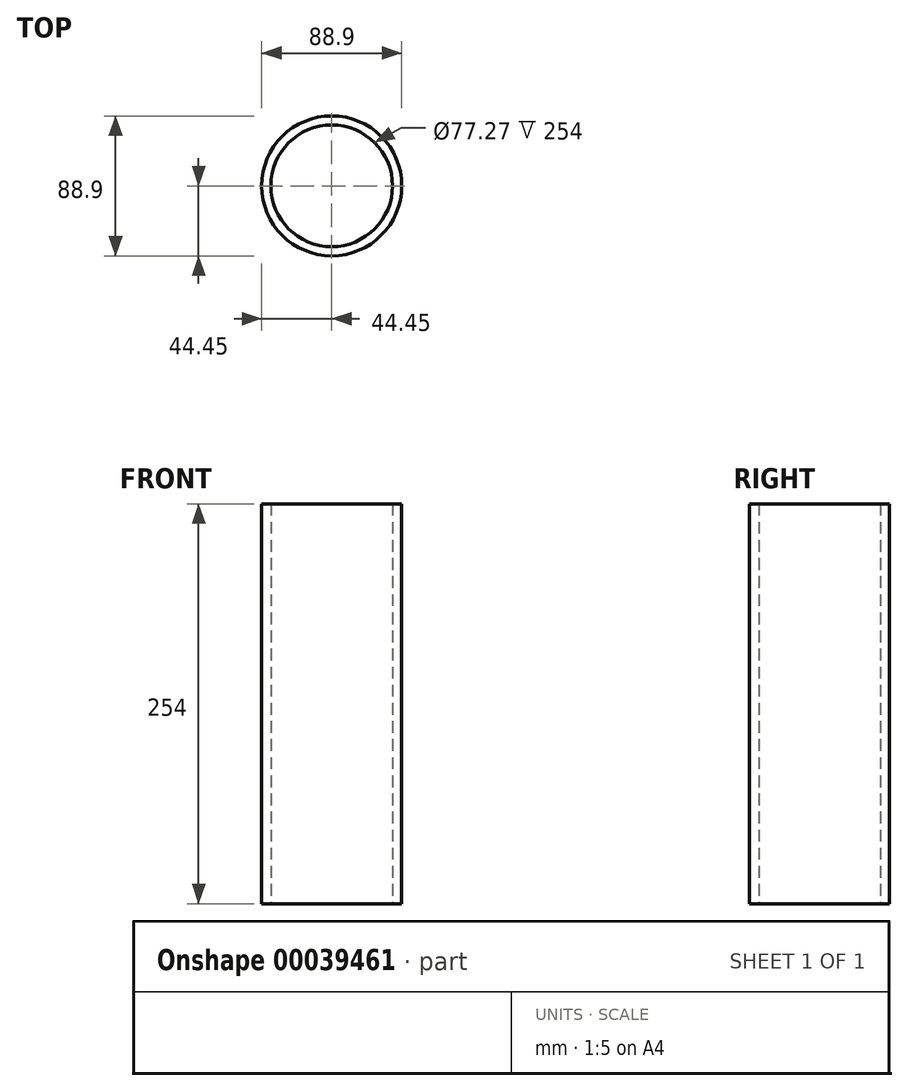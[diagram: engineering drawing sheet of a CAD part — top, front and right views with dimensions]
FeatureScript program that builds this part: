
annotation { "Feature Type Name" : "Feature", "Feature Type Description" : "" }
export const myFeature = defineFeature(function(context is Context, id is Id, definition is map)
    precondition{}
    {
        {
            var Q0;
            Q0=qCreatedBy(makeId("Top.planeOp"),FACE);
            var sketch = newSketch(context, id + "F0", { "sketchPlane" : qUnion([Q0])});
            skCircle(sketch, "E0", {"center": v(0, 0) * mm, "radius": 38.63 * mm});
            skCircle(sketch, "E1", {"center": v(0, 0) * mm, "radius": 44.45 * mm});
            skSolve(sketch);
        }
        {
            var Q0;
            Q0=makeQuery(id+"F0.imprint","IMPRINT",FACE,{"disambiguationData":[TD([[makeQuery(id+"F0.imprint","IMPRINT",EDGE,{"derivedFrom":sQuery(id+"F0.wireOp",EDGE,"E0")}),-1.0]])]});
            extrude(context, id + "F1", {"entities" : qUnion([Q0]), "endBound" : BoundingType.SYMMETRIC, "depth" : 254 * mm});
        }
    });
